# Revit family: Standalone Emergency - 659323SA
name_source: partatom
category: Lighting Fixtures
units: mm (PartAtom-declared; Revit-internal decimal feet)

## family parameters
Cut with Voids When Loaded = Yes
Host = Face
Light Source = Yes
OmniClass Number = 23.80.70.14
OmniClass Title = Luminaries for External Lighting
Part Type = Normal
Room Calculation Point = No
Round Connector Dimension = Use Diameter
Shared = No

## types (4) — shared parameters
Apparent Load = 41 VA
Color Filter = 16777215
Default Elevation = 1200 mm
Depth = 84 mm  [stored 0.275591 ft]
Description = Economy LED Batten- Standalone Emergency - L12 LED Batten
Dimming Lamp Color Temperature Shift = <None>
Emit from Line Length = 1280 mm  [stored 4.19948 ft]
IP_Rating = 20
LampWattage = 37 W
Length = 1280 mm  [stored 4.19948 ft]
LoadClassification = Lighting
Manufacturer = Legrand
Material = Zinc Steel-Powdered Coat
Model = 659323SA
PowerFactor = 0.9
ProductCode = 659323SA
SupplyFrequency = 50 Hz
SupplyVoltage = 240 V
Tilt Angle = 90.00°
URL = http://www.legrand.com.au
Width = 100 mm  [stored 0.328084 ft]

## per-type parameters (varying)
| type | Emergency Light Material | Emergency Light OnOff | Lens Material | Light Source Offset | Photometric Web File | calc_light source |
| 659323SA - Emergency | Opal Polycarbonate-On | Yes | Opal Polycarbonate-Off | 0 mm  [stored 0 ft] | 659323SA_ECO LED BATTEN L12 STANDALONE D50 EMERGENCY MODE.IES | 615 mm |
| 659323SA - Normal - 3000k | Glass-Lens | No | Opal Polycarbonate-On | 45 mm  [stored 0.147638 ft] | 659323SA_ECO LED BATTEN 3K L12 STANDALONE MAINS MODE WITH ONOFF SENSOR.IES | 0 mm  [stored 0 ft] |
| 659323SA - Normal - 4000k | Glass-Lens | No | Opal Polycarbonate-On | 45 mm  [stored 0.147638 ft] | 659323SA_ECO LED BATTEN 4K L12 STANDALONE MAINS MODE WITH ONOFF SENSOR.IES | 0 mm  [stored 0 ft] |
| 659323SA - Normal - 6000k | Glass-Lens | No | Opal Polycarbonate-On | 45 mm  [stored 0.147638 ft] | 659323SA_ECO LED BATTEN 6K L12 STANDALONE MAINS MODE WITH ONOFF SENSOR.IES | 0 mm  [stored 0 ft] |

note: [stored X ft] marks values corroborated as IEEE doubles in the binary element streams (Revit-internal decimal feet)

## geometry (parser evidence)
native form markers: Sweep x8
no freeform markers — native parametric forms only
